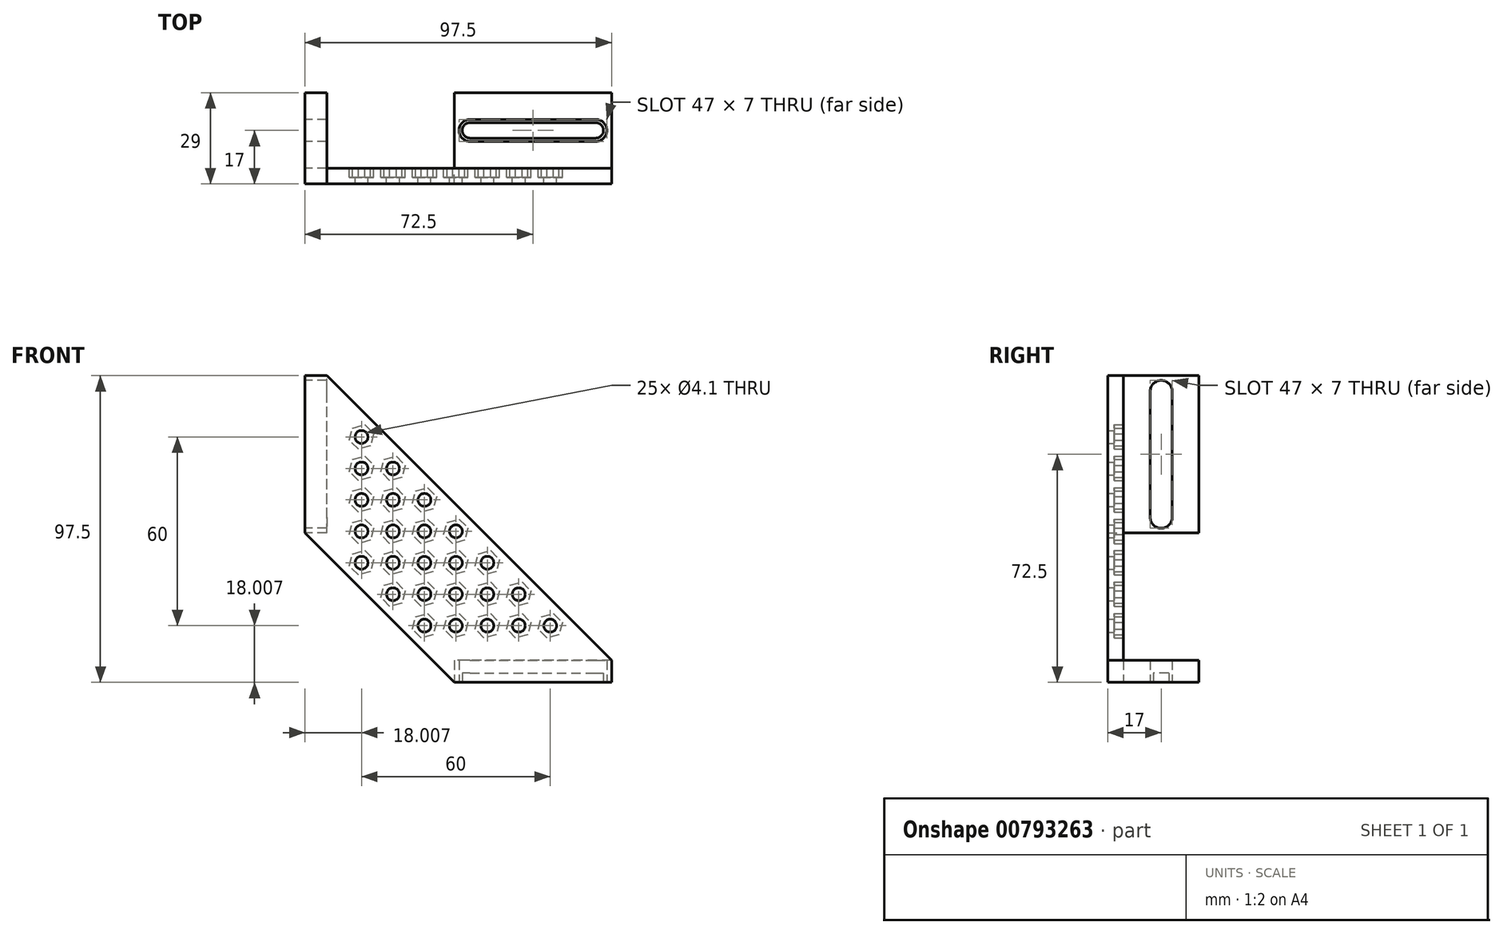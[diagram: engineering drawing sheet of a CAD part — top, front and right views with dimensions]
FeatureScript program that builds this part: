
annotation { "Feature Type Name" : "Feature", "Feature Type Description" : "" }
export const myFeature = defineFeature(function(context is Context, id is Id, definition is map)
    precondition{}
    {
        {
            var Q0;
            Q0=qCreatedBy(makeId("Top.planeOp"),FACE);
            var sketch = newSketch(context, id + "F0", { "sketchPlane" : qUnion([Q0])});
            skLineSegment(sketch, "E0.left", {"start": v(-21, 12) * mm, "end": v(-21, -12) * mm});
            skPoint(sketch, "E0.middle", {"position": v(0, 0) * mm});
            skLineSegment(sketch, "E1", {"start": v(-16, 12) * mm, "end": v(-16, -12) * mm, "construction": true});
            skPoint(sketch, "E2", {"position": v(-16, -8) * mm});
            skPoint(sketch, "E3", {"position": v(0, -8) * mm});
            skPoint(sketch, "E4", {"position": v(-16, 0) * mm});
            skArc(sketch, "E5", {"start": v(-16, -5.95) * mm, "mid": v(-18.05, -8) * mm, "end": v(-16, -10.05) * mm});
            skLineSegment(sketch, "E6", {"start": v(-16, -5.95) * mm, "end": v(0, -5.95) * mm});
            skLineSegment(sketch, "E7.MirrorCS", {"start": v(-16, -10.05) * mm, "end": v(0, -10.05) * mm});
            skArc(sketch, "E8", {"start": v(-16, -2.45) * mm, "mid": v(-18.45, 0) * mm, "end": v(-16, 2.45) * mm});
            skLineSegment(sketch, "E9", {"start": v(-16, -2.45) * mm, "end": v(0, -2.45) * mm});
            skPoint(sketch, "E10.MirrorP", {"position": v(-16, 2.45) * mm});
            skLineSegment(sketch, "E11.MirrorCS", {"start": v(-16, 2.45) * mm, "end": v(0, 2.45) * mm});
            skLineSegment(sketch, "E12.MirrorCS", {"start": v(0, -12) * mm, "end": v(0, 12) * mm, "construction": true});
            skLineSegment(sketch, "E13", {"start": v(-21, -12) * mm, "end": v(0, -12) * mm});
            skLineSegment(sketch, "E14", {"start": v(-21, 0) * mm, "end": v(0, 0) * mm, "construction": true});
            skLineSegment(sketch, "E15", {"start": v(0, -8) * mm, "end": v(-21, -8) * mm, "construction": true});
            skPoint(sketch, "E15.endSnap0", {"position": v(-18.05, -8) * mm});
            skLineSegment(sketch, "E16", {"start": v(0, -12) * mm, "end": v(29, -12) * mm});
            skLineSegment(sketch, "E17", {"start": v(29, -12) * mm, "end": v(29, 12) * mm});
            skLineSegment(sketch, "E18", {"start": v(29, 12) * mm, "end": v(-21, 12) * mm});
            skLineSegment(sketch, "E19", {"start": v(24, 12) * mm, "end": v(24, -12) * mm, "construction": true});
            skLineSegment(sketch, "E20", {"start": v(0, -5.95) * mm, "end": v(24, -5.95) * mm});
            skLineSegment(sketch, "E21", {"start": v(0, -10.05) * mm, "end": v(24, -10.05) * mm});
            skLineSegment(sketch, "E22", {"start": v(0, -2.45) * mm, "end": v(24, -2.45) * mm});
            skLineSegment(sketch, "E23", {"start": v(0, 2.45) * mm, "end": v(24, 2.45) * mm});
            skLineSegment(sketch, "E24", {"start": v(24, 0) * mm, "end": v(0, 0) * mm, "construction": true});
            skLineSegment(sketch, "E25", {"start": v(0, -8) * mm, "end": v(24, -8) * mm, "construction": true});
            skArc(sketch, "E26", {"start": v(24, -2.45) * mm, "mid": v(26.45, 0) * mm, "end": v(24, 2.45) * mm});
            skArc(sketch, "E27", {"start": v(24, -10.05) * mm, "mid": v(26.05, -8) * mm, "end": v(24, -5.95) * mm});
            skLineSegment(sketch, "E28.MirrorCS", {"start": v(0, 5.95) * mm, "end": v(24, 5.95) * mm});
            skLineSegment(sketch, "E29.MirrorCS", {"start": v(0, 10.05) * mm, "end": v(24, 10.05) * mm});
            skLineSegment(sketch, "E30.MirrorCS", {"start": v(-16, 10.05) * mm, "end": v(0, 10.05) * mm});
            skLineSegment(sketch, "E31.MirrorCS", {"start": v(-16, 5.95) * mm, "end": v(0, 5.95) * mm});
            skArc(sketch, "E32.MirrorCS", {"start": v(-16, 5.95) * mm, "mid": v(-18.05, 8) * mm, "end": v(-16, 10.05) * mm});
            skArc(sketch, "E33.MirrorCS", {"start": v(24, 10.05) * mm, "mid": v(26.05, 8) * mm, "end": v(24, 5.95) * mm});
            skArc(sketch, "E34.0", {"start": v(-16, -4.5) * mm, "mid": v(-19.5, -8) * mm, "end": v(-16, -11.5) * mm});
            skLineSegment(sketch, "E34.1", {"start": v(0, -4.5) * mm, "end": v(24, -4.5) * mm});
            skArc(sketch, "E34.2", {"start": v(24, -11.5) * mm, "mid": v(27.5, -8) * mm, "end": v(24, -4.5) * mm});
            skLineSegment(sketch, "E34.3", {"start": v(-16, -4.5) * mm, "end": v(0, -4.5) * mm});
            skLineSegment(sketch, "E34.4", {"start": v(0, -11.5) * mm, "end": v(24, -11.5) * mm});
            skLineSegment(sketch, "E34.5", {"start": v(-16, -11.5) * mm, "end": v(0, -11.5) * mm});
            skArc(sketch, "E35.0", {"start": v(-16, 4.5) * mm, "mid": v(-19.5, 8) * mm, "end": v(-16, 11.5) * mm});
            skLineSegment(sketch, "E35.1", {"start": v(0, 11.5) * mm, "end": v(24, 11.5) * mm});
            skArc(sketch, "E35.2", {"start": v(24, 11.5) * mm, "mid": v(27.5, 8) * mm, "end": v(24, 4.5) * mm});
            skLineSegment(sketch, "E35.3", {"start": v(-16, 11.5) * mm, "end": v(0, 11.5) * mm});
            skLineSegment(sketch, "E35.4", {"start": v(0, 4.5) * mm, "end": v(24, 4.5) * mm});
            skLineSegment(sketch, "E35.5", {"start": v(-16, 4.5) * mm, "end": v(0, 4.5) * mm});
            skArc(sketch, "E36", {"start": v(-16, -3.5) * mm, "mid": v(-19.5, 0) * mm, "end": v(-16, 3.5) * mm});
            skArc(sketch, "E37", {"start": v(24, -3.5) * mm, "mid": v(27.5, 0) * mm, "end": v(24, 3.5) * mm});
            skLineSegment(sketch, "E38", {"start": v(-16, 3.5) * mm, "end": v(24, 3.5) * mm});
            skLineSegment(sketch, "E39", {"start": v(24, -3.5) * mm, "end": v(-16, -3.5) * mm});
            skSolve(sketch);
        }
        {
            var Q0;
            Q0=makeQuery(id+"F0.imprint","IMPRINT",FACE,{"disambiguationData":[TD([[makeQuery(id+"F0.imprint","IMPRINT",EDGE,{"derivedFrom":sQuery(id+"F0.wireOp",EDGE,"E0.left")}),1.0]])]});
            var Q1;
            Q1=makeQuery(id+"F0.imprint","IMPRINT",FACE,{"disambiguationData":[TD([[makeQuery(id+"F0.imprint","IMPRINT",EDGE,{"derivedFrom":sQuery(id+"F0.wireOp",EDGE,"E5")}),1.0]])]});
            var Q2;
            Q2=makeQuery(id+"F0.imprint","IMPRINT",FACE,{"disambiguationData":[TD([[makeQuery(id+"F0.imprint","IMPRINT",EDGE,{"derivedFrom":sQuery(id+"F0.wireOp",EDGE,"E5")}),-1.0]])]});
            var Q3;
            Q3=makeQuery(id+"F0.imprint","IMPRINT",FACE,{"disambiguationData":[TD([[makeQuery(id+"F0.imprint","IMPRINT",EDGE,{"derivedFrom":sQuery(id+"F0.wireOp",EDGE,"E28.MirrorCS")}),-1.0]])]});
            var Q4;
            Q4=makeQuery(id+"F0.imprint","IMPRINT",FACE,{"disambiguationData":[TD([[makeQuery(id+"F0.imprint","IMPRINT",EDGE,{"derivedFrom":sQuery(id+"F0.wireOp",EDGE,"E28.MirrorCS")}),1.0]])]});
            extrude(context, id + "F1", {"entities" : qUnion([Q0, Q1, Q2, Q3, Q4]), "depth" : 7 * mm, "offsetDistance" : 25 * mm});
        }
        {
            var Q0;
            Q0=makeQuery(id+"F0.imprint","IMPRINT",FACE,{"disambiguationData":[TD([[makeQuery(id+"F0.imprint","IMPRINT",EDGE,{"derivedFrom":sQuery(id+"F0.wireOp",EDGE,"E8")}),1.0]])]});
            extrude(context, id + "F2", {"entities" : qUnion([Q0]), "operationType" : NewBodyOperationType.ADD, "depth" : 3 * mm, "offsetDistance" : 25 * mm});
        }
        {
            var Q0;
            Q0=makeQuery(id+"F1.opExtrude","SWEPT_FACE",FACE,{"disambiguationData":[OSD([sQuery(id+"F0.wireOp",EDGE,"E0.left")])]});
            var sketch = newSketch(context, id + "F3", { "sketchPlane" : qUnion([Q0])});
            skLineSegment(sketch, "E40", {"start": v(-12, 3.5) * mm, "end": v(12, 3.5) * mm, "construction": true});
            skSolve(sketch);
        }
        {
            var Q0;
            Q0=makeQuery(id+"F1.opExtrude","SWEPT_BODY",BODY,{"disambiguationData":[OSD([sQuery(id+"F0.wireOp",EDGE,"E0.bottom"),sQuery(id+"F0.wireOp",EDGE,"E0.top"),sQuery(id+"F0.wireOp",EDGE,"E0.left"),sQuery(id+"F0.wireOp",EDGE,"E0.right"),sQuery(id+"F0.wireOp",EDGE,"rf366HtQ-3S43-huQP-rZQL-GLvETnePYKPt"),sQuery(id+"F0.wireOp",EDGE,"72d57c59-205e-4b86-9b7f-fefa83471a3c0.MirrorC"),sQuery(id+"F0.wireOp",EDGE,"3BxVGwLA-TLUy-tZVP-cH0U-NxRYkcQ5ksQi"),sQuery(id+"F0.wireOp",EDGE,"b526d6a5-a937-4610-9a53-f8e406b30c9d0.MirrorC"),sQuery(id+"F0.wireOp",EDGE,"71981b63-6e51-433c-862b-60b74b25135c0.MirrorC"),sQuery(id+"F0.wireOp",EDGE,"b5f8f83e-67df-48da-9f18-6f8bbd20fa1b0.MirrorC"),sQuery(id+"F0.wireOp",EDGE,"1DxgEhBs-8iCY-IMLj-HmtB-05ri525AO9wY"),sQuery(id+"F0.wireOp",EDGE,"NxLUD5A4-VjtB-lD8M-x3iM-VxBEk0lLSaKk"),sQuery(id+"F0.wireOp",EDGE,"3f1f5e11-1e70-4af8-87df-d7b5c765f6460.MirrorC")])]});
            var Q1;
            Q1=sQuery(id+"F3.wireOp",EDGE,"E40");
            transform(context, id + "F4", {"entities" : qUnion([Q0]), "transformType" : TransformType.ROTATION, "transformAxis" : qUnion([Q1]), "angle" : 90 * degree, "makeCopy" : true});
        }
        {
            var Q0;
            Q0=makeQuery(id+"F4.opPattern","COPY",FACE,{"derivedFrom":makeQuery(id+"F1.opExtrude","SWEPT_FACE",FACE,{"disambiguationData":[OSD([sQuery(id+"F0.wireOp",EDGE,"E0.left")])]}),"instanceName":"1"});
            var sketch = newSketch(context, id + "F5", { "sketchPlane" : qUnion([Q0])});
            skLineSegment(sketch, "E41", {"start": v(-21, -12) * mm, "end": v(-21, 12) * mm, "construction": true});
            skPoint(sketch, "E41.startSnap0", {"position": v(-21, -12) * mm});
            skSolve(sketch);
        }
        {
            var Q0;
            Q0=sQuery(id+"F5.wireOp",EDGE,"E41");
            cPlane(context, id + "F6", {"entities" : qUnion([Q0]), "cplaneType" : CPlaneType.LINE_ANGLE, "offset" : 25 * mm, "angle" : 90 * degree, "width" : 150 * mm, "height" : 150 * mm});
        }
        {
            var Q0;
            Q0=qCreatedBy(id+"F6.planeOp",FACE);
            var sketch = newSketch(context, id + "F7", { "sketchPlane" : qUnion([Q0])});
            skLineSegment(sketch, "E42", {"start": v(0, 3.5) * mm, "end": v(0, 53.5) * mm, "construction": true});
            skSolve(sketch);
        }
        {
            var Q0;
            Q0=makeQuery(id+"F4.opPattern","COPY",BODY,{"derivedFrom":makeQuery(id+"F1.opExtrude","SWEPT_BODY",BODY,{"disambiguationData":[OSD([sQuery(id+"F0.wireOp",EDGE,"E0.left"),sQuery(id+"F0.wireOp",EDGE,"E13"),sQuery(id+"F0.wireOp",EDGE,"E16"),sQuery(id+"F0.wireOp",EDGE,"E17"),sQuery(id+"F0.wireOp",EDGE,"E18"),sQuery(id+"F0.wireOp",EDGE,"2010bd3d-8bd0-4ab8-9feb-11eef9d441c0.0"),sQuery(id+"F0.wireOp",EDGE,"2010bd3d-8bd0-4ab8-9feb-11eef9d441c0.1"),sQuery(id+"F0.wireOp",EDGE,"2010bd3d-8bd0-4ab8-9feb-11eef9d441c0.2"),sQuery(id+"F0.wireOp",EDGE,"2010bd3d-8bd0-4ab8-9feb-11eef9d441c0.3"),sQuery(id+"F0.wireOp",EDGE,"2010bd3d-8bd0-4ab8-9feb-11eef9d441c0.4"),sQuery(id+"F0.wireOp",EDGE,"2010bd3d-8bd0-4ab8-9feb-11eef9d441c0.5")])]}),"instanceName":"1"});
            var Q1;
            Q1=sQuery(id+"F7.wireOp",EDGE,"E42");
            transform(context, id + "F8", {"entities" : qUnion([Q0]), "transformType" : TransformType.ROTATION, "transformAxis" : qUnion([Q1]), "angle" : 180 * degree, "makeCopy" : false});
        }
        {
            var Q0;
            Q0=makeQuery(id+"F4.opPattern","COPY",BODY,{"derivedFrom":makeQuery(id+"F1.opExtrude","SWEPT_BODY",BODY,{"disambiguationData":[OSD([sQuery(id+"F0.wireOp",EDGE,"E0.bottom"),sQuery(id+"F0.wireOp",EDGE,"E0.top"),sQuery(id+"F0.wireOp",EDGE,"E0.left"),sQuery(id+"F0.wireOp",EDGE,"E0.right"),sQuery(id+"F0.wireOp",EDGE,"rf366HtQ-3S43-huQP-rZQL-GLvETnePYKPt"),sQuery(id+"F0.wireOp",EDGE,"72d57c59-205e-4b86-9b7f-fefa83471a3c0.MirrorC"),sQuery(id+"F0.wireOp",EDGE,"3BxVGwLA-TLUy-tZVP-cH0U-NxRYkcQ5ksQi"),sQuery(id+"F0.wireOp",EDGE,"b526d6a5-a937-4610-9a53-f8e406b30c9d0.MirrorC"),sQuery(id+"F0.wireOp",EDGE,"71981b63-6e51-433c-862b-60b74b25135c0.MirrorC"),sQuery(id+"F0.wireOp",EDGE,"b5f8f83e-67df-48da-9f18-6f8bbd20fa1b0.MirrorC"),sQuery(id+"F0.wireOp",EDGE,"1DxgEhBs-8iCY-IMLj-HmtB-05ri525AO9wY"),sQuery(id+"F0.wireOp",EDGE,"NxLUD5A4-VjtB-lD8M-x3iM-VxBEk0lLSaKk"),sQuery(id+"F0.wireOp",EDGE,"3f1f5e11-1e70-4af8-87df-d7b5c765f6460.MirrorC")])]}),"instanceName":"1"});
            var Q1;
            Q1=qCreatedBy(makeId("Top.planeOp"),FACE);
            transform(context, id + "F9", {"entities" : qUnion([Q0]), "transformType" : TransformType.TRANSLATION_DISTANCE, "transformDirection" : qUnion([Q1]), "distance" : 44 * mm, "makeCopy" : false});
        }
        {
            var Q0;
            Q0=makeQuery(id+"F4.opPattern","COPY",BODY,{"derivedFrom":makeQuery(id+"F1.opExtrude","SWEPT_BODY",BODY,{"disambiguationData":[OSD([sQuery(id+"F0.wireOp",EDGE,"E0.bottom"),sQuery(id+"F0.wireOp",EDGE,"E0.top"),sQuery(id+"F0.wireOp",EDGE,"E0.left"),sQuery(id+"F0.wireOp",EDGE,"E0.right"),sQuery(id+"F0.wireOp",EDGE,"rf366HtQ-3S43-huQP-rZQL-GLvETnePYKPt"),sQuery(id+"F0.wireOp",EDGE,"72d57c59-205e-4b86-9b7f-fefa83471a3c0.MirrorC"),sQuery(id+"F0.wireOp",EDGE,"3BxVGwLA-TLUy-tZVP-cH0U-NxRYkcQ5ksQi"),sQuery(id+"F0.wireOp",EDGE,"b526d6a5-a937-4610-9a53-f8e406b30c9d0.MirrorC"),sQuery(id+"F0.wireOp",EDGE,"71981b63-6e51-433c-862b-60b74b25135c0.MirrorC"),sQuery(id+"F0.wireOp",EDGE,"b5f8f83e-67df-48da-9f18-6f8bbd20fa1b0.MirrorC"),sQuery(id+"F0.wireOp",EDGE,"1DxgEhBs-8iCY-IMLj-HmtB-05ri525AO9wY"),sQuery(id+"F0.wireOp",EDGE,"NxLUD5A4-VjtB-lD8M-x3iM-VxBEk0lLSaKk"),sQuery(id+"F0.wireOp",EDGE,"3f1f5e11-1e70-4af8-87df-d7b5c765f6460.MirrorC")])]}),"instanceName":"1"});
            var Q1;
            Q1=qCreatedBy(makeId("Right.planeOp"),FACE);
            transform(context, id + "F10", {"entities" : qUnion([Q0]), "transformType" : TransformType.TRANSLATION_DISTANCE, "transformDirection" : qUnion([Q1]), "distance" : 44 * mm, "oppositeDirection" : true, "makeCopy" : false});
        }
        {
            var Q0;
            Q0=sQuery(id+"F0.wireOp",VERTEX,"E0.left.end");
            var Q1;
            Q1=makeQuery(id+"F4.opPattern","COPY",VERTEX,{"derivedFrom":makeQuery(id+"F1.opExtrude","CAP_VERTEX",VERTEX,{"disambiguationData":[OSD([sQuery(id+"F0.wireOp",EDGE,"E0.left"),sQuery(id+"F0.wireOp",EDGE,"E18")])],"isStart":true}),"instanceName":"1"});
            var Q2;
            Q2=makeQuery(id+"F4.opPattern","COPY",VERTEX,{"derivedFrom":makeQuery(id+"F1.opExtrude","CAP_VERTEX",VERTEX,{"disambiguationData":[OSD([sQuery(id+"F0.wireOp",EDGE,"E0.left"),sQuery(id+"F0.wireOp",EDGE,"E18")])],"isStart":false}),"instanceName":"1"});
            cPlane(context, id + "F11", {"entities" : qUnion([Q0, Q1, Q2]), "cplaneType" : CPlaneType.THREE_POINT, "offset" : 25 * mm, "width" : 150 * mm, "height" : 150 * mm});
        }
        {
            var Q0;
            Q0=qCreatedBy(id+"F11.planeOp",FACE);
            var sketch = newSketch(context, id + "F12", { "sketchPlane" : qUnion([Q0])});
            skLineSegment(sketch, "E43", {"start": v(-21, 0) * mm, "end": v(-68.5, 47.5) * mm});
            skLineSegment(sketch, "E44", {"start": v(-61.5, 97.5) * mm, "end": v(29, 7) * mm});
            skLineSegment(sketch, "E45", {"start": v(-68.5, 47.5) * mm, "end": v(-68.5, 97.5) * mm});
            skLineSegment(sketch, "E46", {"start": v(-61.5, 97.5) * mm, "end": v(-68.5, 97.5) * mm});
            skLineSegment(sketch, "E47", {"start": v(-21, 0) * mm, "end": v(29, 0) * mm});
            skLineSegment(sketch, "E48", {"start": v(29, 0) * mm, "end": v(29, 7) * mm});
            skLineSegment(sketch, "E49", {"start": v(-68.5, 97.5) * mm, "end": v(-61.5, 97.5) * mm});
            skPoint(sketch, "E50", {"position": v(-20.5, 48) * mm});
            skCircle(sketch, "E51", {"center": v(-20.5, 48) * mm, "radius": 2.05 * mm});
            skCircle(sketch, "E52.cCircle", {"center": v(-20.5, 48) * mm, "radius": 4 * mm, "construction": true});
            skLineSegment(sketch, "E52.0", {"start": v(-23.32, 50.84) * mm, "end": v(-19.46, 51.87) * mm});
            skLineSegment(sketch, "E52.1", {"start": v(-19.46, 51.87) * mm, "end": v(-16.63, 49.04) * mm});
            skLineSegment(sketch, "E52.2", {"start": v(-16.63, 49.04) * mm, "end": v(-17.66, 45.18) * mm});
            skLineSegment(sketch, "E52.3", {"start": v(-17.66, 45.18) * mm, "end": v(-21.53, 44.14) * mm});
            skLineSegment(sketch, "E52.4", {"start": v(-21.53, 44.14) * mm, "end": v(-24.36, 46.97) * mm});
            skLineSegment(sketch, "E52.5", {"start": v(-24.36, 46.97) * mm, "end": v(-23.32, 50.84) * mm});
            skLineSegment(sketch, "E53", {"start": v(-44.75, 23.75) * mm, "end": v(-16.25, 52.25) * mm, "construction": true});
            skLineSegment(sketch, "E54", {"start": v(-68.5, 47.5) * mm, "end": v(-68.5, 0) * mm, "construction": true});
            skLineSegment(sketch, "E55", {"start": v(-68.5, 0) * mm, "end": v(-21, 0) * mm, "construction": true});
            skLineSegment(sketch, "E56", {"start": v(-21, 7) * mm, "end": v(-68.5, 7) * mm, "construction": true});
            skLineSegment(sketch, "E57", {"start": v(-68.5, 7) * mm, "end": v(-68.5, 47.5) * mm, "construction": true});
            skLineSegment(sketch, "E58", {"start": v(-53.5, 89.5) * mm, "end": v(-53.5, 15) * mm, "construction": true});
            skLineSegment(sketch, "E59", {"start": v(-53.5, 15) * mm, "end": v(21, 15) * mm, "construction": true});
            skPoint(sketch, "E60", {"position": v(-17.66, 50.84) * mm});
            skLineSegment(sketch, "E61", {"start": v(-20.5, 48) * mm, "end": v(-20.5, 15) * mm, "construction": true});
            skLineSegment(sketch, "E62", {"start": v(-20.5, 48) * mm, "end": v(-53.5, 48) * mm, "construction": true});
            skPoint(sketch, "E63", {"position": v(-20.5, 38) * mm});
            skCircle(sketch, "E64", {"center": v(-20.5, 38) * mm, "radius": 2.05 * mm});
            skCircle(sketch, "E65.cCircle", {"center": v(-20.5, 38) * mm, "radius": 4 * mm, "construction": true});
            skLineSegment(sketch, "E65.0", {"start": v(-23.32, 40.84) * mm, "end": v(-19.46, 41.87) * mm});
            skLineSegment(sketch, "E65.1", {"start": v(-19.46, 41.87) * mm, "end": v(-16.63, 39.04) * mm});
            skLineSegment(sketch, "E65.2", {"start": v(-16.63, 39.04) * mm, "end": v(-17.66, 35.18) * mm});
            skLineSegment(sketch, "E65.3", {"start": v(-17.66, 35.18) * mm, "end": v(-21.53, 34.14) * mm});
            skLineSegment(sketch, "E65.4", {"start": v(-21.53, 34.14) * mm, "end": v(-24.36, 36.97) * mm});
            skLineSegment(sketch, "E65.5", {"start": v(-24.36, 36.97) * mm, "end": v(-23.32, 40.84) * mm});
            skPoint(sketch, "E66", {"position": v(-30.5, 48) * mm});
            skCircle(sketch, "E67", {"center": v(-30.5, 48) * mm, "radius": 2.05 * mm});
            skCircle(sketch, "E68.cCircle", {"center": v(-30.5, 48) * mm, "radius": 4 * mm, "construction": true});
            skLineSegment(sketch, "E68.0", {"start": v(-33.32, 50.84) * mm, "end": v(-29.46, 51.87) * mm});
            skLineSegment(sketch, "E68.1", {"start": v(-29.46, 51.87) * mm, "end": v(-26.63, 49.04) * mm});
            skLineSegment(sketch, "E68.2", {"start": v(-26.63, 49.04) * mm, "end": v(-27.66, 45.18) * mm});
            skLineSegment(sketch, "E68.3", {"start": v(-27.66, 45.18) * mm, "end": v(-31.53, 44.14) * mm});
            skLineSegment(sketch, "E68.4", {"start": v(-31.53, 44.14) * mm, "end": v(-34.36, 46.97) * mm});
            skLineSegment(sketch, "E68.5", {"start": v(-34.36, 46.97) * mm, "end": v(-33.32, 50.84) * mm});
            skPoint(sketch, "E69", {"position": v(-30.5, 38) * mm});
            skCircle(sketch, "E70", {"center": v(-30.5, 38) * mm, "radius": 2.05 * mm});
            skCircle(sketch, "E71.cCircle", {"center": v(-30.5, 38) * mm, "radius": 4 * mm, "construction": true});
            skLineSegment(sketch, "E71.0", {"start": v(-33.32, 40.84) * mm, "end": v(-29.46, 41.87) * mm});
            skLineSegment(sketch, "E71.1", {"start": v(-29.46, 41.87) * mm, "end": v(-26.63, 39.04) * mm});
            skLineSegment(sketch, "E71.2", {"start": v(-26.63, 39.04) * mm, "end": v(-27.66, 35.18) * mm});
            skLineSegment(sketch, "E71.3", {"start": v(-27.66, 35.18) * mm, "end": v(-31.53, 34.14) * mm});
            skLineSegment(sketch, "E71.4", {"start": v(-31.53, 34.14) * mm, "end": v(-34.36, 36.97) * mm});
            skLineSegment(sketch, "E71.5", {"start": v(-34.36, 36.97) * mm, "end": v(-33.32, 40.84) * mm});
            skLineSegment(sketch, "E72", {"start": v(-20.5, 38) * mm, "end": v(-2, 38) * mm, "construction": true});
            skLineSegment(sketch, "E73", {"start": v(-30.5, 48) * mm, "end": v(-30.5, 66.5) * mm, "construction": true});
            skPoint(sketch, "E74", {"position": v(-10.5, 38) * mm});
            skCircle(sketch, "E75", {"center": v(-10.5, 38) * mm, "radius": 2.05 * mm});
            skCircle(sketch, "E76.cCircle", {"center": v(-10.5, 38) * mm, "radius": 4 * mm, "construction": true});
            skLineSegment(sketch, "E76.0", {"start": v(-13.32, 40.84) * mm, "end": v(-9.46, 41.87) * mm});
            skLineSegment(sketch, "E76.1", {"start": v(-9.46, 41.87) * mm, "end": v(-6.63, 39.04) * mm});
            skLineSegment(sketch, "E76.2", {"start": v(-6.63, 39.04) * mm, "end": v(-7.66, 35.18) * mm});
            skLineSegment(sketch, "E76.3", {"start": v(-7.66, 35.18) * mm, "end": v(-11.53, 34.14) * mm});
            skLineSegment(sketch, "E76.4", {"start": v(-11.53, 34.14) * mm, "end": v(-14.36, 36.97) * mm});
            skLineSegment(sketch, "E76.5", {"start": v(-14.36, 36.97) * mm, "end": v(-13.32, 40.84) * mm});
            skPoint(sketch, "E77", {"position": v(-30.5, 58) * mm});
            skCircle(sketch, "E78", {"center": v(-30.5, 58) * mm, "radius": 2.05 * mm});
            skCircle(sketch, "E79.cCircle", {"center": v(-30.5, 58) * mm, "radius": 4 * mm, "construction": true});
            skLineSegment(sketch, "E79.0", {"start": v(-33.32, 60.84) * mm, "end": v(-29.46, 61.87) * mm});
            skLineSegment(sketch, "E79.1", {"start": v(-29.46, 61.87) * mm, "end": v(-26.63, 59.04) * mm});
            skLineSegment(sketch, "E79.2", {"start": v(-26.63, 59.04) * mm, "end": v(-27.66, 55.18) * mm});
            skLineSegment(sketch, "E79.3", {"start": v(-27.66, 55.18) * mm, "end": v(-31.53, 54.14) * mm});
            skLineSegment(sketch, "E79.4", {"start": v(-31.53, 54.14) * mm, "end": v(-34.36, 56.97) * mm});
            skLineSegment(sketch, "E79.5", {"start": v(-34.36, 56.97) * mm, "end": v(-33.32, 60.84) * mm});
            skPoint(sketch, "E80", {"position": v(-40.5, 48) * mm});
            skCircle(sketch, "E81", {"center": v(-40.5, 48) * mm, "radius": 2.05 * mm});
            skCircle(sketch, "E82.cCircle", {"center": v(-40.5, 48) * mm, "radius": 4 * mm, "construction": true});
            skLineSegment(sketch, "E82.0", {"start": v(-43.32, 50.84) * mm, "end": v(-39.46, 51.87) * mm});
            skLineSegment(sketch, "E82.1", {"start": v(-39.46, 51.87) * mm, "end": v(-36.63, 49.04) * mm});
            skLineSegment(sketch, "E82.2", {"start": v(-36.63, 49.04) * mm, "end": v(-37.66, 45.18) * mm});
            skLineSegment(sketch, "E82.3", {"start": v(-37.66, 45.18) * mm, "end": v(-41.53, 44.14) * mm});
            skLineSegment(sketch, "E82.4", {"start": v(-41.53, 44.14) * mm, "end": v(-44.36, 46.97) * mm});
            skLineSegment(sketch, "E82.5", {"start": v(-44.36, 46.97) * mm, "end": v(-43.32, 50.84) * mm});
            skPoint(sketch, "E83", {"position": v(-40.5, 38) * mm});
            skCircle(sketch, "E84", {"center": v(-40.5, 38) * mm, "radius": 2.05 * mm});
            skCircle(sketch, "E85.cCircle", {"center": v(-40.5, 38) * mm, "radius": 4 * mm, "construction": true});
            skLineSegment(sketch, "E85.0", {"start": v(-43.32, 40.84) * mm, "end": v(-39.46, 41.87) * mm});
            skLineSegment(sketch, "E85.1", {"start": v(-39.46, 41.87) * mm, "end": v(-36.63, 39.04) * mm});
            skLineSegment(sketch, "E85.2", {"start": v(-36.63, 39.04) * mm, "end": v(-37.66, 35.18) * mm});
            skLineSegment(sketch, "E85.3", {"start": v(-37.66, 35.18) * mm, "end": v(-41.53, 34.14) * mm});
            skLineSegment(sketch, "E85.4", {"start": v(-41.53, 34.14) * mm, "end": v(-44.36, 36.97) * mm});
            skLineSegment(sketch, "E85.5", {"start": v(-44.36, 36.97) * mm, "end": v(-43.32, 40.84) * mm});
            skPoint(sketch, "E86", {"position": v(-40.5, 58) * mm});
            skCircle(sketch, "E87", {"center": v(-40.5, 58) * mm, "radius": 2.05 * mm});
            skCircle(sketch, "E88.cCircle", {"center": v(-40.5, 58) * mm, "radius": 4 * mm, "construction": true});
            skLineSegment(sketch, "E88.0", {"start": v(-43.32, 60.84) * mm, "end": v(-39.46, 61.87) * mm});
            skLineSegment(sketch, "E88.1", {"start": v(-39.46, 61.87) * mm, "end": v(-36.63, 59.04) * mm});
            skLineSegment(sketch, "E88.2", {"start": v(-36.63, 59.04) * mm, "end": v(-37.66, 55.18) * mm});
            skLineSegment(sketch, "E88.3", {"start": v(-37.66, 55.18) * mm, "end": v(-41.53, 54.14) * mm});
            skLineSegment(sketch, "E88.4", {"start": v(-41.53, 54.14) * mm, "end": v(-44.36, 56.97) * mm});
            skLineSegment(sketch, "E88.5", {"start": v(-44.36, 56.97) * mm, "end": v(-43.32, 60.84) * mm});
            skLineSegment(sketch, "E89", {"start": v(-40.5, 76.5) * mm, "end": v(-40.5, 28) * mm, "construction": true});
            skPoint(sketch, "E90", {"position": v(-20.5, 28) * mm});
            skCircle(sketch, "E91", {"center": v(-20.5, 28) * mm, "radius": 2.05 * mm});
            skCircle(sketch, "E92.cCircle", {"center": v(-20.5, 28) * mm, "radius": 4 * mm, "construction": true});
            skLineSegment(sketch, "E92.0", {"start": v(-23.32, 30.84) * mm, "end": v(-19.46, 31.87) * mm});
            skLineSegment(sketch, "E92.1", {"start": v(-19.46, 31.87) * mm, "end": v(-16.63, 29.04) * mm});
            skLineSegment(sketch, "E92.2", {"start": v(-16.63, 29.04) * mm, "end": v(-17.66, 25.18) * mm});
            skLineSegment(sketch, "E92.3", {"start": v(-17.66, 25.18) * mm, "end": v(-21.53, 24.14) * mm});
            skLineSegment(sketch, "E92.4", {"start": v(-21.53, 24.14) * mm, "end": v(-24.36, 26.97) * mm});
            skLineSegment(sketch, "E92.5", {"start": v(-24.36, 26.97) * mm, "end": v(-23.32, 30.84) * mm});
            skPoint(sketch, "E93", {"position": v(-30.5, 28) * mm});
            skCircle(sketch, "E94", {"center": v(-30.5, 28) * mm, "radius": 2.05 * mm});
            skCircle(sketch, "E95.cCircle", {"center": v(-30.5, 28) * mm, "radius": 4 * mm, "construction": true});
            skLineSegment(sketch, "E95.0", {"start": v(-33.32, 30.84) * mm, "end": v(-29.46, 31.87) * mm});
            skLineSegment(sketch, "E95.1", {"start": v(-29.46, 31.87) * mm, "end": v(-26.63, 29.04) * mm});
            skLineSegment(sketch, "E95.2", {"start": v(-26.63, 29.04) * mm, "end": v(-27.66, 25.18) * mm});
            skLineSegment(sketch, "E95.3", {"start": v(-27.66, 25.18) * mm, "end": v(-31.53, 24.14) * mm});
            skLineSegment(sketch, "E95.4", {"start": v(-31.53, 24.14) * mm, "end": v(-34.36, 26.97) * mm});
            skLineSegment(sketch, "E95.5", {"start": v(-34.36, 26.97) * mm, "end": v(-33.32, 30.84) * mm});
            skPoint(sketch, "E96", {"position": v(-10.5, 28) * mm});
            skCircle(sketch, "E97", {"center": v(-10.5, 28) * mm, "radius": 2.05 * mm});
            skCircle(sketch, "E98.cCircle", {"center": v(-10.5, 28) * mm, "radius": 4 * mm, "construction": true});
            skLineSegment(sketch, "E98.0", {"start": v(-13.32, 30.84) * mm, "end": v(-9.46, 31.87) * mm});
            skLineSegment(sketch, "E98.1", {"start": v(-9.46, 31.87) * mm, "end": v(-6.63, 29.04) * mm});
            skLineSegment(sketch, "E98.2", {"start": v(-6.63, 29.04) * mm, "end": v(-7.66, 25.18) * mm});
            skLineSegment(sketch, "E98.3", {"start": v(-7.66, 25.18) * mm, "end": v(-11.53, 24.14) * mm});
            skLineSegment(sketch, "E98.4", {"start": v(-11.53, 24.14) * mm, "end": v(-14.36, 26.97) * mm});
            skLineSegment(sketch, "E98.5", {"start": v(-14.36, 26.97) * mm, "end": v(-13.32, 30.84) * mm});
            skPoint(sketch, "E99", {"position": v(-40.5, 28) * mm});
            skCircle(sketch, "E100", {"center": v(-40.5, 28) * mm, "radius": 2.05 * mm});
            skCircle(sketch, "E101.cCircle", {"center": v(-40.5, 28) * mm, "radius": 4 * mm, "construction": true});
            skLineSegment(sketch, "E101.0", {"start": v(-43.32, 30.84) * mm, "end": v(-39.46, 31.87) * mm});
            skLineSegment(sketch, "E101.1", {"start": v(-39.46, 31.87) * mm, "end": v(-36.63, 29.04) * mm});
            skLineSegment(sketch, "E101.2", {"start": v(-36.63, 29.04) * mm, "end": v(-37.66, 25.18) * mm});
            skLineSegment(sketch, "E101.3", {"start": v(-37.66, 25.18) * mm, "end": v(-41.53, 24.14) * mm});
            skLineSegment(sketch, "E101.4", {"start": v(-41.53, 24.14) * mm, "end": v(-44.36, 26.97) * mm});
            skLineSegment(sketch, "E101.5", {"start": v(-44.36, 26.97) * mm, "end": v(-43.32, 30.84) * mm});
            skLineSegment(sketch, "E102", {"start": v(8, 28) * mm, "end": v(-40.5, 28) * mm, "construction": true});
            skPoint(sketch, "E103", {"position": v(-40.5, 68) * mm});
            skCircle(sketch, "E104", {"center": v(-40.5, 68) * mm, "radius": 2.05 * mm});
            skCircle(sketch, "E105.cCircle", {"center": v(-40.5, 68) * mm, "radius": 4 * mm, "construction": true});
            skLineSegment(sketch, "E105.0", {"start": v(-44.36, 66.97) * mm, "end": v(-43.32, 70.84) * mm});
            skLineSegment(sketch, "E105.1", {"start": v(-43.32, 70.84) * mm, "end": v(-39.46, 71.87) * mm});
            skLineSegment(sketch, "E105.2", {"start": v(-39.46, 71.87) * mm, "end": v(-36.63, 69.04) * mm});
            skLineSegment(sketch, "E105.3", {"start": v(-36.63, 69.04) * mm, "end": v(-37.66, 65.18) * mm});
            skLineSegment(sketch, "E105.4", {"start": v(-37.66, 65.18) * mm, "end": v(-41.53, 64.14) * mm});
            skLineSegment(sketch, "E105.5", {"start": v(-41.53, 64.14) * mm, "end": v(-44.36, 66.97) * mm});
            skPoint(sketch, "E106", {"position": v(-0.5, 28) * mm});
            skCircle(sketch, "E107", {"center": v(-0.5, 28) * mm, "radius": 2.05 * mm});
            skCircle(sketch, "E108.cCircle", {"center": v(-0.5, 28) * mm, "radius": 4 * mm, "construction": true});
            skLineSegment(sketch, "E108.0", {"start": v(-3.32, 30.84) * mm, "end": v(0.54, 31.87) * mm});
            skLineSegment(sketch, "E108.1", {"start": v(0.54, 31.87) * mm, "end": v(3.37, 29.04) * mm});
            skLineSegment(sketch, "E108.2", {"start": v(3.37, 29.04) * mm, "end": v(2.34, 25.18) * mm});
            skLineSegment(sketch, "E108.3", {"start": v(2.34, 25.18) * mm, "end": v(-1.53, 24.14) * mm});
            skLineSegment(sketch, "E108.4", {"start": v(-1.53, 24.14) * mm, "end": v(-4.36, 26.97) * mm});
            skLineSegment(sketch, "E108.5", {"start": v(-4.36, 26.97) * mm, "end": v(-3.32, 30.84) * mm});
            skPoint(sketch, "E109", {"position": v(-10.5, 18) * mm});
            skCircle(sketch, "E110", {"center": v(-10.5, 18) * mm, "radius": 2.05 * mm});
            skCircle(sketch, "E111.cCircle", {"center": v(-10.5, 18) * mm, "radius": 4 * mm, "construction": true});
            skLineSegment(sketch, "E111.0", {"start": v(-13.32, 20.84) * mm, "end": v(-9.46, 21.87) * mm});
            skLineSegment(sketch, "E111.1", {"start": v(-9.46, 21.87) * mm, "end": v(-6.63, 19.04) * mm});
            skLineSegment(sketch, "E111.2", {"start": v(-6.63, 19.04) * mm, "end": v(-7.66, 15.18) * mm});
            skLineSegment(sketch, "E111.3", {"start": v(-7.66, 15.18) * mm, "end": v(-11.53, 14.14) * mm});
            skLineSegment(sketch, "E111.4", {"start": v(-11.53, 14.14) * mm, "end": v(-14.36, 16.97) * mm});
            skLineSegment(sketch, "E111.5", {"start": v(-14.36, 16.97) * mm, "end": v(-13.32, 20.84) * mm});
            skPoint(sketch, "E112", {"position": v(-20.5, 18) * mm});
            skCircle(sketch, "E113", {"center": v(-20.5, 18) * mm, "radius": 2.05 * mm});
            skCircle(sketch, "E114.cCircle", {"center": v(-20.5, 18) * mm, "radius": 4 * mm, "construction": true});
            skLineSegment(sketch, "E114.0", {"start": v(-23.32, 20.84) * mm, "end": v(-19.46, 21.87) * mm});
            skLineSegment(sketch, "E114.1", {"start": v(-19.46, 21.87) * mm, "end": v(-16.63, 19.04) * mm});
            skLineSegment(sketch, "E114.2", {"start": v(-16.63, 19.04) * mm, "end": v(-17.66, 15.18) * mm});
            skLineSegment(sketch, "E114.3", {"start": v(-17.66, 15.18) * mm, "end": v(-21.53, 14.14) * mm});
            skLineSegment(sketch, "E114.4", {"start": v(-21.53, 14.14) * mm, "end": v(-24.36, 16.97) * mm});
            skLineSegment(sketch, "E114.5", {"start": v(-24.36, 16.97) * mm, "end": v(-23.32, 20.84) * mm});
            skPoint(sketch, "E115", {"position": v(-0.5, 18) * mm});
            skCircle(sketch, "E116", {"center": v(-0.5, 18) * mm, "radius": 2.05 * mm});
            skCircle(sketch, "E117.cCircle", {"center": v(-0.5, 18) * mm, "radius": 4 * mm, "construction": true});
            skLineSegment(sketch, "E117.0", {"start": v(-3.32, 20.84) * mm, "end": v(0.54, 21.87) * mm});
            skLineSegment(sketch, "E117.1", {"start": v(0.54, 21.87) * mm, "end": v(3.37, 19.04) * mm});
            skLineSegment(sketch, "E117.2", {"start": v(3.37, 19.04) * mm, "end": v(2.34, 15.18) * mm});
            skLineSegment(sketch, "E117.3", {"start": v(2.34, 15.18) * mm, "end": v(-1.53, 14.14) * mm});
            skLineSegment(sketch, "E117.4", {"start": v(-1.53, 14.14) * mm, "end": v(-4.36, 16.97) * mm});
            skLineSegment(sketch, "E117.5", {"start": v(-4.36, 16.97) * mm, "end": v(-3.32, 20.84) * mm});
            skPoint(sketch, "E118", {"position": v(-30.5, 18) * mm});
            skCircle(sketch, "E119", {"center": v(-30.5, 18) * mm, "radius": 2.05 * mm});
            skCircle(sketch, "E120.cCircle", {"center": v(-30.5, 18) * mm, "radius": 4 * mm, "construction": true});
            skLineSegment(sketch, "E120.0", {"start": v(-33.32, 20.84) * mm, "end": v(-29.46, 21.87) * mm});
            skLineSegment(sketch, "E120.1", {"start": v(-29.46, 21.87) * mm, "end": v(-26.63, 19.04) * mm});
            skLineSegment(sketch, "E120.2", {"start": v(-26.63, 19.04) * mm, "end": v(-27.66, 15.18) * mm});
            skLineSegment(sketch, "E120.3", {"start": v(-27.66, 15.18) * mm, "end": v(-31.53, 14.14) * mm});
            skLineSegment(sketch, "E120.4", {"start": v(-31.53, 14.14) * mm, "end": v(-34.36, 16.97) * mm});
            skLineSegment(sketch, "E120.5", {"start": v(-34.36, 16.97) * mm, "end": v(-33.32, 20.84) * mm});
            skLineSegment(sketch, "E121", {"start": v(18, 18) * mm, "end": v(-39, 18) * mm, "construction": true});
            skPoint(sketch, "E122", {"position": v(9.5, 18) * mm});
            skCircle(sketch, "E123", {"center": v(9.5, 18) * mm, "radius": 2.05 * mm});
            skCircle(sketch, "E124.cCircle", {"center": v(9.5, 18) * mm, "radius": 4 * mm, "construction": true});
            skLineSegment(sketch, "E124.0", {"start": v(5.64, 16.97) * mm, "end": v(6.68, 20.84) * mm});
            skLineSegment(sketch, "E124.1", {"start": v(6.68, 20.84) * mm, "end": v(10.54, 21.87) * mm});
            skLineSegment(sketch, "E124.2", {"start": v(10.54, 21.87) * mm, "end": v(13.37, 19.04) * mm});
            skLineSegment(sketch, "E124.3", {"start": v(13.37, 19.04) * mm, "end": v(12.34, 15.18) * mm});
            skLineSegment(sketch, "E124.4", {"start": v(12.34, 15.18) * mm, "end": v(8.47, 14.14) * mm});
            skLineSegment(sketch, "E124.5", {"start": v(8.47, 14.14) * mm, "end": v(5.64, 16.97) * mm});
            skPoint(sketch, "E125", {"position": v(-50.5, 58) * mm});
            skCircle(sketch, "E126", {"center": v(-50.5, 58) * mm, "radius": 2.05 * mm});
            skCircle(sketch, "E127.cCircle", {"center": v(-50.5, 58) * mm, "radius": 4 * mm, "construction": true});
            skLineSegment(sketch, "E127.0", {"start": v(-53.32, 60.84) * mm, "end": v(-49.46, 61.87) * mm});
            skLineSegment(sketch, "E127.1", {"start": v(-49.46, 61.87) * mm, "end": v(-46.63, 59.04) * mm});
            skLineSegment(sketch, "E127.2", {"start": v(-46.63, 59.04) * mm, "end": v(-47.66, 55.18) * mm});
            skLineSegment(sketch, "E127.3", {"start": v(-47.66, 55.18) * mm, "end": v(-51.53, 54.14) * mm});
            skLineSegment(sketch, "E127.4", {"start": v(-51.53, 54.14) * mm, "end": v(-54.36, 56.97) * mm});
            skLineSegment(sketch, "E127.5", {"start": v(-54.36, 56.97) * mm, "end": v(-53.32, 60.84) * mm});
            skPoint(sketch, "E128", {"position": v(-50.5, 48) * mm});
            skCircle(sketch, "E129", {"center": v(-50.5, 48) * mm, "radius": 2.05 * mm});
            skCircle(sketch, "E130.cCircle", {"center": v(-50.5, 48) * mm, "radius": 4 * mm, "construction": true});
            skLineSegment(sketch, "E130.0", {"start": v(-53.32, 50.84) * mm, "end": v(-49.46, 51.87) * mm});
            skLineSegment(sketch, "E130.1", {"start": v(-49.46, 51.87) * mm, "end": v(-46.63, 49.04) * mm});
            skLineSegment(sketch, "E130.2", {"start": v(-46.63, 49.04) * mm, "end": v(-47.66, 45.18) * mm});
            skLineSegment(sketch, "E130.3", {"start": v(-47.66, 45.18) * mm, "end": v(-51.53, 44.14) * mm});
            skLineSegment(sketch, "E130.4", {"start": v(-51.53, 44.14) * mm, "end": v(-54.36, 46.97) * mm});
            skLineSegment(sketch, "E130.5", {"start": v(-54.36, 46.97) * mm, "end": v(-53.32, 50.84) * mm});
            skPoint(sketch, "E131", {"position": v(-50.5, 68) * mm});
            skCircle(sketch, "E132", {"center": v(-50.5, 68) * mm, "radius": 2.05 * mm});
            skCircle(sketch, "E133.cCircle", {"center": v(-50.5, 68) * mm, "radius": 4 * mm, "construction": true});
            skLineSegment(sketch, "E133.0", {"start": v(-53.32, 70.84) * mm, "end": v(-49.46, 71.87) * mm});
            skLineSegment(sketch, "E133.1", {"start": v(-49.46, 71.87) * mm, "end": v(-46.63, 69.04) * mm});
            skLineSegment(sketch, "E133.2", {"start": v(-46.63, 69.04) * mm, "end": v(-47.66, 65.18) * mm});
            skLineSegment(sketch, "E133.3", {"start": v(-47.66, 65.18) * mm, "end": v(-51.53, 64.14) * mm});
            skLineSegment(sketch, "E133.4", {"start": v(-51.53, 64.14) * mm, "end": v(-54.36, 66.97) * mm});
            skLineSegment(sketch, "E133.5", {"start": v(-54.36, 66.97) * mm, "end": v(-53.32, 70.84) * mm});
            skPoint(sketch, "E134", {"position": v(-50.5, 38) * mm});
            skCircle(sketch, "E135", {"center": v(-50.5, 38) * mm, "radius": 2.05 * mm});
            skCircle(sketch, "E136.cCircle", {"center": v(-50.5, 38) * mm, "radius": 4 * mm, "construction": true});
            skLineSegment(sketch, "E136.0", {"start": v(-53.32, 40.84) * mm, "end": v(-49.46, 41.87) * mm});
            skLineSegment(sketch, "E136.1", {"start": v(-49.46, 41.87) * mm, "end": v(-46.63, 39.04) * mm});
            skLineSegment(sketch, "E136.2", {"start": v(-46.63, 39.04) * mm, "end": v(-47.66, 35.18) * mm});
            skLineSegment(sketch, "E136.3", {"start": v(-47.66, 35.18) * mm, "end": v(-51.53, 34.14) * mm});
            skLineSegment(sketch, "E136.4", {"start": v(-51.53, 34.14) * mm, "end": v(-54.36, 36.97) * mm});
            skLineSegment(sketch, "E136.5", {"start": v(-54.36, 36.97) * mm, "end": v(-53.32, 40.84) * mm});
            skPoint(sketch, "E137", {"position": v(-50.5, 78) * mm});
            skCircle(sketch, "E138", {"center": v(-50.5, 78) * mm, "radius": 2.05 * mm});
            skCircle(sketch, "E139.cCircle", {"center": v(-50.5, 78) * mm, "radius": 4 * mm, "construction": true});
            skLineSegment(sketch, "E139.0", {"start": v(-54.36, 76.97) * mm, "end": v(-53.32, 80.84) * mm});
            skLineSegment(sketch, "E139.1", {"start": v(-53.32, 80.84) * mm, "end": v(-49.46, 81.87) * mm});
            skLineSegment(sketch, "E139.2", {"start": v(-49.46, 81.87) * mm, "end": v(-46.63, 79.04) * mm});
            skLineSegment(sketch, "E139.3", {"start": v(-46.63, 79.04) * mm, "end": v(-47.66, 75.18) * mm});
            skLineSegment(sketch, "E139.4", {"start": v(-47.66, 75.18) * mm, "end": v(-51.53, 74.14) * mm});
            skLineSegment(sketch, "E139.5", {"start": v(-51.53, 74.14) * mm, "end": v(-54.36, 76.97) * mm});
            skLineSegment(sketch, "E140", {"start": v(-50.5, 86.5) * mm, "end": v(-50.5, 29.5) * mm, "construction": true});
            skSolve(sketch);
        }
        {
            var Q0;
            Q0=makeQuery(id+"F12.imprint","IMPRINT",FACE,{"disambiguationData":[TD([[makeQuery(id+"F12.imprint","IMPRINT",EDGE,{"derivedFrom":sQuery(id+"F12.wireOp",EDGE,"E44")}),-1.0]])]});
            var Q1;
            Q1=makeQuery(id+"F12.imprint","IMPRINT",FACE,{"disambiguationData":[TD([[makeQuery(id+"F12.imprint","IMPRINT",EDGE,{"derivedFrom":sQuery(id+"F12.wireOp",EDGE,"544cc5c5-56e9-462e-aa7d-0e891712fb88")}),-1.0]])]});
            var Q2;
            Q2=makeQuery(id+"F12.imprint","IMPRINT",FACE,{"disambiguationData":[TD([[makeQuery(id+"F12.imprint","IMPRINT",EDGE,{"derivedFrom":sQuery(id+"F12.wireOp",EDGE,"af930993-f983-4d4b-806c-d5d714f01deb")}),-1.0]])]});
            var Q3;
            Q3=makeQuery(id+"F12.imprint","IMPRINT",FACE,{"disambiguationData":[TD([[makeQuery(id+"F12.imprint","IMPRINT",EDGE,{"derivedFrom":sQuery(id+"F12.wireOp",EDGE,"E51")}),-1.0]])]});
            var Q4;
            Q4=makeQuery(id+"F12.imprint","IMPRINT",FACE,{"disambiguationData":[TD([[makeQuery(id+"F12.imprint","IMPRINT",EDGE,{"derivedFrom":sQuery(id+"F12.wireOp",EDGE,"db4000d2-28b7-4ce0-b6f8-efe2c8e47721")}),-1.0]])]});
            var Q5;
            Q5=makeQuery(id+"F12.imprint","IMPRINT",FACE,{"disambiguationData":[TD([[makeQuery(id+"F12.imprint","IMPRINT",EDGE,{"derivedFrom":sQuery(id+"F12.wireOp",EDGE,"6fd45c98-9014-41e2-a4b9-07c20c1fc8f4")}),-1.0]])]});
            var Q6;
            {var subQ0=sQuery(id+"F12.wireOp",EDGE,"36f95dd1-a930-4b05-802e-2328d4aa170c.1");Q6=makeQuery(id+"F12.imprint","IMPRINT",FACE,{"disambiguationData":[TD([[makeQuery(id+"F12.imprint","IMPRINT",EDGE,{"derivedFrom":subQ0}),-1.0]])]});}
            var Q7;
            Q7=makeQuery(id+"F12.imprint","IMPRINT",FACE,{"disambiguationData":[TD([[makeQuery(id+"F12.imprint","IMPRINT",EDGE,{"derivedFrom":sQuery(id+"F12.wireOp",EDGE,"0217be3f-f015-4376-87de-3fac7a7125e00.MirrorCS")}),1.0]])]});
            var Q8;
            Q8=makeQuery(id+"F12.imprint","IMPRINT",FACE,{"disambiguationData":[TD([[makeQuery(id+"F12.imprint","IMPRINT",EDGE,{"derivedFrom":sQuery(id+"F12.wireOp",EDGE,"3a05cbfe-0b2f-41ad-9fce-b7c3e8f461170.MirrorCS")}),1.0]])]});
            var Q9;
            Q9=makeQuery(id+"F12.imprint","IMPRINT",FACE,{"disambiguationData":[TD([[makeQuery(id+"F12.imprint","IMPRINT",EDGE,{"derivedFrom":sQuery(id+"F12.wireOp",EDGE,"686798c7-8504-4800-9966-571d6854760d0.MirrorCS")}),1.0]])]});
            var Q10;
            Q10=makeQuery(id+"F12.imprint","IMPRINT",FACE,{"disambiguationData":[TD([[makeQuery(id+"F12.imprint","IMPRINT",EDGE,{"derivedFrom":sQuery(id+"F12.wireOp",EDGE,"ee1293b9-60a1-4feb-baa6-848b5ec06ea80.MirrorCS")}),1.0]])]});
            var Q11;
            Q11=makeQuery(id+"F12.imprint","IMPRINT",FACE,{"disambiguationData":[TD([[makeQuery(id+"F12.imprint","IMPRINT",EDGE,{"derivedFrom":sQuery(id+"F12.wireOp",EDGE,"E78")}),-1.0]])]});
            var Q12;
            Q12=makeQuery(id+"F12.imprint","IMPRINT",FACE,{"disambiguationData":[TD([[makeQuery(id+"F12.imprint","IMPRINT",EDGE,{"derivedFrom":sQuery(id+"F12.wireOp",EDGE,"E67")}),-1.0]])]});
            var Q13;
            Q13=makeQuery(id+"F12.imprint","IMPRINT",FACE,{"disambiguationData":[TD([[makeQuery(id+"F12.imprint","IMPRINT",EDGE,{"derivedFrom":sQuery(id+"F12.wireOp",EDGE,"E70")}),-1.0]])]});
            var Q14;
            Q14=makeQuery(id+"F12.imprint","IMPRINT",FACE,{"disambiguationData":[TD([[makeQuery(id+"F12.imprint","IMPRINT",EDGE,{"derivedFrom":sQuery(id+"F12.wireOp",EDGE,"E64")}),-1.0]])]});
            var Q15;
            Q15=makeQuery(id+"F12.imprint","IMPRINT",FACE,{"disambiguationData":[TD([[makeQuery(id+"F12.imprint","IMPRINT",EDGE,{"derivedFrom":sQuery(id+"F12.wireOp",EDGE,"E75")}),-1.0]])]});
            var Q16;
            Q16=makeQuery(id+"F12.imprint","IMPRINT",FACE,{"disambiguationData":[TD([[makeQuery(id+"F12.imprint","IMPRINT",EDGE,{"derivedFrom":sQuery(id+"F12.wireOp",EDGE,"E104")}),-1.0]])]});
            var Q17;
            Q17=makeQuery(id+"F12.imprint","IMPRINT",FACE,{"disambiguationData":[TD([[makeQuery(id+"F12.imprint","IMPRINT",EDGE,{"derivedFrom":sQuery(id+"F12.wireOp",EDGE,"E87")}),-1.0]])]});
            var Q18;
            Q18=makeQuery(id+"F12.imprint","IMPRINT",FACE,{"disambiguationData":[TD([[makeQuery(id+"F12.imprint","IMPRINT",EDGE,{"derivedFrom":sQuery(id+"F12.wireOp",EDGE,"E81")}),-1.0]])]});
            var Q19;
            Q19=makeQuery(id+"F12.imprint","IMPRINT",FACE,{"disambiguationData":[TD([[makeQuery(id+"F12.imprint","IMPRINT",EDGE,{"derivedFrom":sQuery(id+"F12.wireOp",EDGE,"E84")}),-1.0]])]});
            var Q20;
            Q20=makeQuery(id+"F12.imprint","IMPRINT",FACE,{"disambiguationData":[TD([[makeQuery(id+"F12.imprint","IMPRINT",EDGE,{"derivedFrom":sQuery(id+"F12.wireOp",EDGE,"E100")}),-1.0]])]});
            var Q21;
            Q21=makeQuery(id+"F12.imprint","IMPRINT",FACE,{"disambiguationData":[TD([[makeQuery(id+"F12.imprint","IMPRINT",EDGE,{"derivedFrom":sQuery(id+"F12.wireOp",EDGE,"E94")}),-1.0]])]});
            var Q22;
            Q22=makeQuery(id+"F12.imprint","IMPRINT",FACE,{"disambiguationData":[TD([[makeQuery(id+"F12.imprint","IMPRINT",EDGE,{"derivedFrom":sQuery(id+"F12.wireOp",EDGE,"E91")}),-1.0]])]});
            var Q23;
            Q23=makeQuery(id+"F12.imprint","IMPRINT",FACE,{"disambiguationData":[TD([[makeQuery(id+"F12.imprint","IMPRINT",EDGE,{"derivedFrom":sQuery(id+"F12.wireOp",EDGE,"E97")}),-1.0]])]});
            var Q24;
            Q24=makeQuery(id+"F12.imprint","IMPRINT",FACE,{"disambiguationData":[TD([[makeQuery(id+"F12.imprint","IMPRINT",EDGE,{"derivedFrom":sQuery(id+"F12.wireOp",EDGE,"E107")}),-1.0]])]});
            var Q25;
            Q25=makeQuery(id+"F12.imprint","IMPRINT",FACE,{"disambiguationData":[TD([[makeQuery(id+"F12.imprint","IMPRINT",EDGE,{"derivedFrom":sQuery(id+"F12.wireOp",EDGE,"E126")}),-1.0]])]});
            var Q26;
            Q26=makeQuery(id+"F12.imprint","IMPRINT",FACE,{"disambiguationData":[TD([[makeQuery(id+"F12.imprint","IMPRINT",EDGE,{"derivedFrom":sQuery(id+"F12.wireOp",EDGE,"E132")}),-1.0]])]});
            var Q27;
            Q27=makeQuery(id+"F12.imprint","IMPRINT",FACE,{"disambiguationData":[TD([[makeQuery(id+"F12.imprint","IMPRINT",EDGE,{"derivedFrom":sQuery(id+"F12.wireOp",EDGE,"E138")}),-1.0]])]});
            var Q28;
            Q28=makeQuery(id+"F12.imprint","IMPRINT",FACE,{"disambiguationData":[TD([[makeQuery(id+"F12.imprint","IMPRINT",EDGE,{"derivedFrom":sQuery(id+"F12.wireOp",EDGE,"E129")}),-1.0]])]});
            var Q29;
            Q29=makeQuery(id+"F12.imprint","IMPRINT",FACE,{"disambiguationData":[TD([[makeQuery(id+"F12.imprint","IMPRINT",EDGE,{"derivedFrom":sQuery(id+"F12.wireOp",EDGE,"E135")}),-1.0]])]});
            var Q30;
            Q30=makeQuery(id+"F12.imprint","IMPRINT",FACE,{"disambiguationData":[TD([[makeQuery(id+"F12.imprint","IMPRINT",EDGE,{"derivedFrom":sQuery(id+"F12.wireOp",EDGE,"E119")}),-1.0]])]});
            var Q31;
            Q31=makeQuery(id+"F12.imprint","IMPRINT",FACE,{"disambiguationData":[TD([[makeQuery(id+"F12.imprint","IMPRINT",EDGE,{"derivedFrom":sQuery(id+"F12.wireOp",EDGE,"E113")}),-1.0]])]});
            var Q32;
            Q32=makeQuery(id+"F12.imprint","IMPRINT",FACE,{"disambiguationData":[TD([[makeQuery(id+"F12.imprint","IMPRINT",EDGE,{"derivedFrom":sQuery(id+"F12.wireOp",EDGE,"E110")}),-1.0]])]});
            var Q33;
            Q33=makeQuery(id+"F12.imprint","IMPRINT",FACE,{"disambiguationData":[TD([[makeQuery(id+"F12.imprint","IMPRINT",EDGE,{"derivedFrom":sQuery(id+"F12.wireOp",EDGE,"E116")}),-1.0]])]});
            var Q34;
            Q34=makeQuery(id+"F12.imprint","IMPRINT",FACE,{"disambiguationData":[TD([[makeQuery(id+"F12.imprint","IMPRINT",EDGE,{"derivedFrom":sQuery(id+"F12.wireOp",EDGE,"E123")}),-1.0]])]});
            extrude(context, id + "F13", {"entities" : qUnion([Q0, Q1, Q2, Q3, Q4, Q5, Q6, Q7, Q8, Q9, Q10, Q11, Q12, Q13, Q14, Q15, Q16, Q17, Q18, Q19, Q20, Q21, Q22, Q23, Q24, Q25, Q26, Q27, Q28, Q29, Q30, Q31, Q32, Q33, Q34]), "operationType" : NewBodyOperationType.ADD, "depth" : 5 * mm, "offsetDistance" : 25 * mm});
        }
        {
            var Q0;
            Q0=makeQuery(id+"F12.imprint","IMPRINT",FACE,{"disambiguationData":[TD([[makeQuery(id+"F12.imprint","IMPRINT",EDGE,{"derivedFrom":sQuery(id+"F12.wireOp",EDGE,"E51")}),-1.0]])]});
            var Q1;
            Q1=makeQuery(id+"F12.imprint","IMPRINT",FACE,{"disambiguationData":[TD([[makeQuery(id+"F12.imprint","IMPRINT",EDGE,{"derivedFrom":sQuery(id+"F12.wireOp",EDGE,"af930993-f983-4d4b-806c-d5d714f01deb")}),-1.0]])]});
            var Q2;
            Q2=makeQuery(id+"F12.imprint","IMPRINT",FACE,{"disambiguationData":[TD([[makeQuery(id+"F12.imprint","IMPRINT",EDGE,{"derivedFrom":sQuery(id+"F12.wireOp",EDGE,"544cc5c5-56e9-462e-aa7d-0e891712fb88")}),-1.0]])]});
            var Q3;
            Q3=makeQuery(id+"F12.imprint","IMPRINT",FACE,{"disambiguationData":[TD([[makeQuery(id+"F12.imprint","IMPRINT",EDGE,{"derivedFrom":sQuery(id+"F12.wireOp",EDGE,"a7fd36b7-951d-469d-bd4a-abdf8a5abec4")}),-1.0]])]});
            var Q4;
            Q4=makeQuery(id+"F12.imprint","IMPRINT",FACE,{"disambiguationData":[TD([[makeQuery(id+"F12.imprint","IMPRINT",EDGE,{"derivedFrom":sQuery(id+"F12.wireOp",EDGE,"db4000d2-28b7-4ce0-b6f8-efe2c8e47721")}),-1.0]])]});
            var Q5;
            Q5=makeQuery(id+"F12.imprint","IMPRINT",FACE,{"disambiguationData":[TD([[makeQuery(id+"F12.imprint","IMPRINT",EDGE,{"derivedFrom":sQuery(id+"F12.wireOp",EDGE,"6fd45c98-9014-41e2-a4b9-07c20c1fc8f4")}),-1.0]])]});
            var Q6;
            Q6=makeQuery(id+"F12.imprint","IMPRINT",FACE,{"disambiguationData":[TD([[makeQuery(id+"F12.imprint","IMPRINT",EDGE,{"derivedFrom":sQuery(id+"F12.wireOp",EDGE,"0217be3f-f015-4376-87de-3fac7a7125e00.MirrorCS")}),1.0]])]});
            var Q7;
            Q7=makeQuery(id+"F12.imprint","IMPRINT",FACE,{"disambiguationData":[TD([[makeQuery(id+"F12.imprint","IMPRINT",EDGE,{"derivedFrom":sQuery(id+"F12.wireOp",EDGE,"3a05cbfe-0b2f-41ad-9fce-b7c3e8f461170.MirrorCS")}),1.0]])]});
            var Q8;
            Q8=makeQuery(id+"F12.imprint","IMPRINT",FACE,{"disambiguationData":[TD([[makeQuery(id+"F12.imprint","IMPRINT",EDGE,{"derivedFrom":sQuery(id+"F12.wireOp",EDGE,"686798c7-8504-4800-9966-571d6854760d0.MirrorCS")}),1.0]])]});
            var Q9;
            Q9=makeQuery(id+"F12.imprint","IMPRINT",FACE,{"disambiguationData":[TD([[makeQuery(id+"F12.imprint","IMPRINT",EDGE,{"derivedFrom":sQuery(id+"F12.wireOp",EDGE,"ee1293b9-60a1-4feb-baa6-848b5ec06ea80.MirrorCS")}),1.0]])]});
            var Q10;
            Q10=makeQuery(id+"F12.imprint","IMPRINT",FACE,{"disambiguationData":[TD([[makeQuery(id+"F12.imprint","IMPRINT",EDGE,{"derivedFrom":sQuery(id+"F12.wireOp",EDGE,"E75")}),-1.0]])]});
            var Q11;
            Q11=makeQuery(id+"F12.imprint","IMPRINT",FACE,{"disambiguationData":[TD([[makeQuery(id+"F12.imprint","IMPRINT",EDGE,{"derivedFrom":sQuery(id+"F12.wireOp",EDGE,"E64")}),-1.0]])]});
            var Q12;
            Q12=makeQuery(id+"F12.imprint","IMPRINT",FACE,{"disambiguationData":[TD([[makeQuery(id+"F12.imprint","IMPRINT",EDGE,{"derivedFrom":sQuery(id+"F12.wireOp",EDGE,"E70")}),-1.0]])]});
            var Q13;
            Q13=makeQuery(id+"F12.imprint","IMPRINT",FACE,{"disambiguationData":[TD([[makeQuery(id+"F12.imprint","IMPRINT",EDGE,{"derivedFrom":sQuery(id+"F12.wireOp",EDGE,"E67")}),-1.0]])]});
            var Q14;
            Q14=makeQuery(id+"F12.imprint","IMPRINT",FACE,{"disambiguationData":[TD([[makeQuery(id+"F12.imprint","IMPRINT",EDGE,{"derivedFrom":sQuery(id+"F12.wireOp",EDGE,"E78")}),-1.0]])]});
            var Q15;
            Q15=makeQuery(id+"F12.imprint","IMPRINT",FACE,{"disambiguationData":[TD([[makeQuery(id+"F12.imprint","IMPRINT",EDGE,{"derivedFrom":sQuery(id+"F12.wireOp",EDGE,"E107")}),-1.0]])]});
            var Q16;
            Q16=makeQuery(id+"F12.imprint","IMPRINT",FACE,{"disambiguationData":[TD([[makeQuery(id+"F12.imprint","IMPRINT",EDGE,{"derivedFrom":sQuery(id+"F12.wireOp",EDGE,"E97")}),-1.0]])]});
            var Q17;
            Q17=makeQuery(id+"F12.imprint","IMPRINT",FACE,{"disambiguationData":[TD([[makeQuery(id+"F12.imprint","IMPRINT",EDGE,{"derivedFrom":sQuery(id+"F12.wireOp",EDGE,"E91")}),-1.0]])]});
            var Q18;
            Q18=makeQuery(id+"F12.imprint","IMPRINT",FACE,{"disambiguationData":[TD([[makeQuery(id+"F12.imprint","IMPRINT",EDGE,{"derivedFrom":sQuery(id+"F12.wireOp",EDGE,"E94")}),-1.0]])]});
            var Q19;
            Q19=makeQuery(id+"F12.imprint","IMPRINT",FACE,{"disambiguationData":[TD([[makeQuery(id+"F12.imprint","IMPRINT",EDGE,{"derivedFrom":sQuery(id+"F12.wireOp",EDGE,"E100")}),-1.0]])]});
            var Q20;
            Q20=makeQuery(id+"F12.imprint","IMPRINT",FACE,{"disambiguationData":[TD([[makeQuery(id+"F12.imprint","IMPRINT",EDGE,{"derivedFrom":sQuery(id+"F12.wireOp",EDGE,"E84")}),-1.0]])]});
            var Q21;
            Q21=makeQuery(id+"F12.imprint","IMPRINT",FACE,{"disambiguationData":[TD([[makeQuery(id+"F12.imprint","IMPRINT",EDGE,{"derivedFrom":sQuery(id+"F12.wireOp",EDGE,"E81")}),-1.0]])]});
            var Q22;
            Q22=makeQuery(id+"F12.imprint","IMPRINT",FACE,{"disambiguationData":[TD([[makeQuery(id+"F12.imprint","IMPRINT",EDGE,{"derivedFrom":sQuery(id+"F12.wireOp",EDGE,"E87")}),-1.0]])]});
            var Q23;
            Q23=makeQuery(id+"F12.imprint","IMPRINT",FACE,{"disambiguationData":[TD([[makeQuery(id+"F12.imprint","IMPRINT",EDGE,{"derivedFrom":sQuery(id+"F12.wireOp",EDGE,"E104")}),-1.0]])]});
            var Q24;
            Q24=makeQuery(id+"F12.imprint","IMPRINT",FACE,{"disambiguationData":[TD([[makeQuery(id+"F12.imprint","IMPRINT",EDGE,{"derivedFrom":sQuery(id+"F12.wireOp",EDGE,"E138")}),-1.0]])]});
            var Q25;
            Q25=makeQuery(id+"F12.imprint","IMPRINT",FACE,{"disambiguationData":[TD([[makeQuery(id+"F12.imprint","IMPRINT",EDGE,{"derivedFrom":sQuery(id+"F12.wireOp",EDGE,"E132")}),-1.0]])]});
            var Q26;
            Q26=makeQuery(id+"F12.imprint","IMPRINT",FACE,{"disambiguationData":[TD([[makeQuery(id+"F12.imprint","IMPRINT",EDGE,{"derivedFrom":sQuery(id+"F12.wireOp",EDGE,"E126")}),-1.0]])]});
            var Q27;
            Q27=makeQuery(id+"F12.imprint","IMPRINT",FACE,{"disambiguationData":[TD([[makeQuery(id+"F12.imprint","IMPRINT",EDGE,{"derivedFrom":sQuery(id+"F12.wireOp",EDGE,"E129")}),-1.0]])]});
            var Q28;
            Q28=makeQuery(id+"F12.imprint","IMPRINT",FACE,{"disambiguationData":[TD([[makeQuery(id+"F12.imprint","IMPRINT",EDGE,{"derivedFrom":sQuery(id+"F12.wireOp",EDGE,"E135")}),-1.0]])]});
            var Q29;
            Q29=makeQuery(id+"F12.imprint","IMPRINT",FACE,{"disambiguationData":[TD([[makeQuery(id+"F12.imprint","IMPRINT",EDGE,{"derivedFrom":sQuery(id+"F12.wireOp",EDGE,"E119")}),-1.0]])]});
            var Q30;
            Q30=makeQuery(id+"F12.imprint","IMPRINT",FACE,{"disambiguationData":[TD([[makeQuery(id+"F12.imprint","IMPRINT",EDGE,{"derivedFrom":sQuery(id+"F12.wireOp",EDGE,"E113")}),-1.0]])]});
            var Q31;
            Q31=makeQuery(id+"F12.imprint","IMPRINT",FACE,{"disambiguationData":[TD([[makeQuery(id+"F12.imprint","IMPRINT",EDGE,{"derivedFrom":sQuery(id+"F12.wireOp",EDGE,"E110")}),-1.0]])]});
            var Q32;
            Q32=makeQuery(id+"F12.imprint","IMPRINT",FACE,{"disambiguationData":[TD([[makeQuery(id+"F12.imprint","IMPRINT",EDGE,{"derivedFrom":sQuery(id+"F12.wireOp",EDGE,"E116")}),-1.0]])]});
            var Q33;
            Q33=makeQuery(id+"F12.imprint","IMPRINT",FACE,{"disambiguationData":[TD([[makeQuery(id+"F12.imprint","IMPRINT",EDGE,{"derivedFrom":sQuery(id+"F12.wireOp",EDGE,"E123")}),-1.0]])]});
            extrude(context, id + "F14", {"entities" : qUnion([Q0, Q1, Q2, Q3, Q4, Q5, Q6, Q7, Q8, Q9, Q10, Q11, Q12, Q13, Q14, Q15, Q16, Q17, Q18, Q19, Q20, Q21, Q22, Q23, Q24, Q25, Q26, Q27, Q28, Q29, Q30, Q31, Q32, Q33]), "operationType" : NewBodyOperationType.REMOVE, "depth" : 3 * mm, "offsetDistance" : 25 * mm});
        }
    });
